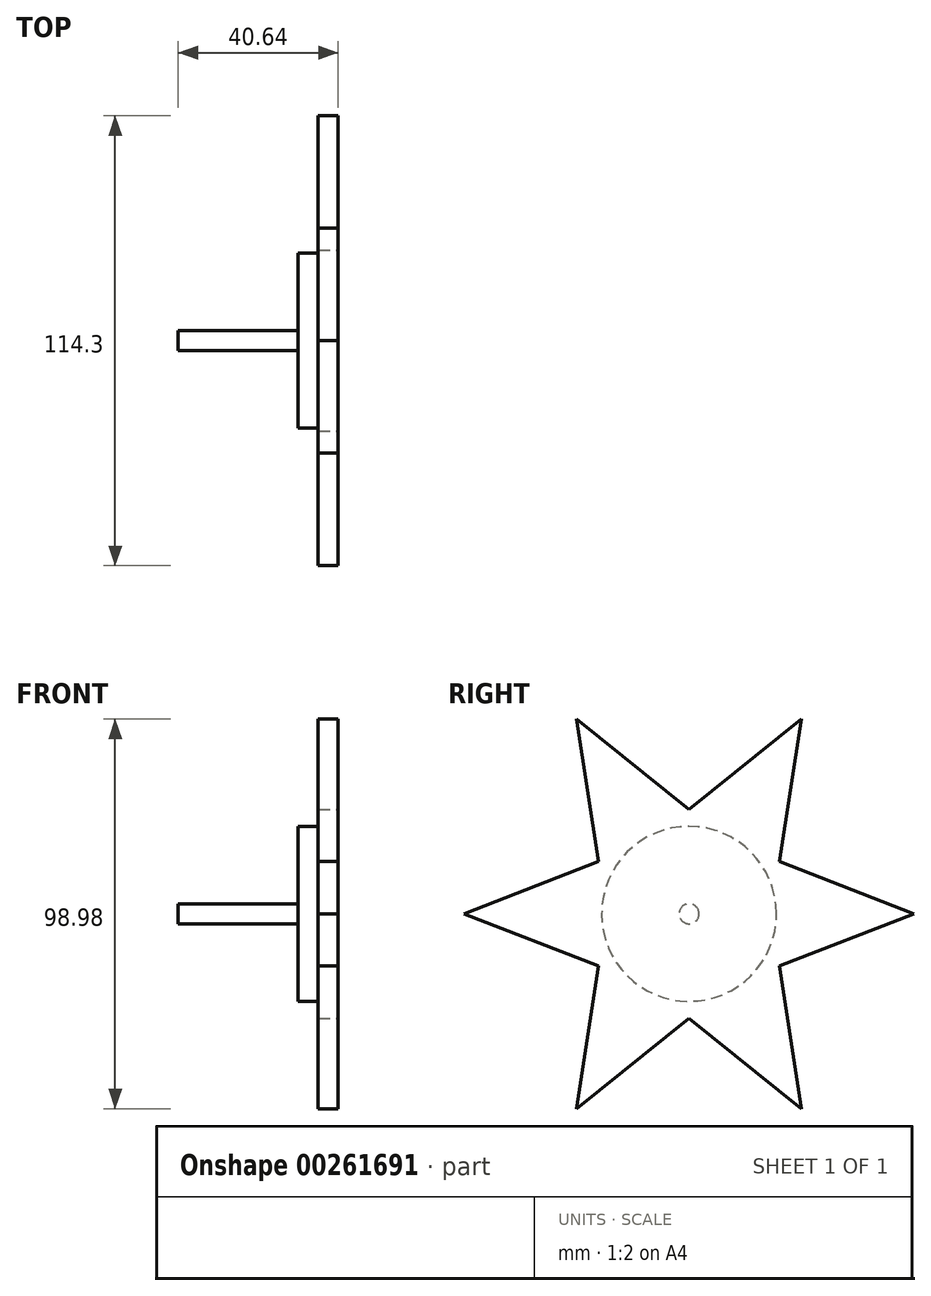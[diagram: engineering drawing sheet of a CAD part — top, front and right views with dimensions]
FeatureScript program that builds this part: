
annotation { "Feature Type Name" : "Feature", "Feature Type Description" : "" }
export const myFeature = defineFeature(function(context is Context, id is Id, definition is map)
    precondition{}
    {
        {
            var Q0;
            Q0=qCreatedBy(makeId("Right.planeOp"),FACE);
            var sketch = newSketch(context, id + "F0", { "sketchPlane" : qUnion([Q0])});
            skLineSegment(sketch, "E0", {"start": v(57.15, 0) * mm, "end": v(-57.15, 0) * mm});
            skCircle(sketch, "E1", {"center": v(0, 0) * mm, "radius": 2.54 * mm});
            skCircle(sketch, "E2", {"center": v(0, 0) * mm, "radius": 22.23 * mm});
            skCircle(sketch, "E3", {"center": v(0, 0) * mm, "radius": 57.15 * mm});
            skLineSegment(sketch, "E4", {"start": v(-57.15, 0) * mm, "end": v(0, 22.23) * mm});
            skLineSegment(sketch, "E5", {"start": v(0, 22.23) * mm, "end": v(57.15, 0) * mm});
            skLineSegment(sketch, "E6", {"start": v(57.15, 0) * mm, "end": v(0, -22.23) * mm});
            skLineSegment(sketch, "E7", {"start": v(0, -22.23) * mm, "end": v(-57.15, 0) * mm});
            skLineSegment(sketch, "E8", {"start": v(19.25, 11.11) * mm, "end": v(-28.57, 49.5) * mm});
            skLineSegment(sketch, "E9", {"start": v(-28.57, 49.5) * mm, "end": v(-19.25, -11.11) * mm});
            skLineSegment(sketch, "E10", {"start": v(-19.25, -11.11) * mm, "end": v(28.57, -49.5) * mm});
            skLineSegment(sketch, "E11", {"start": v(28.57, -49.5) * mm, "end": v(19.25, 11.11) * mm});
            skLineSegment(sketch, "E12", {"start": v(-28.57, 49.5) * mm, "end": v(28.57, -49.5) * mm});
            skLineSegment(sketch, "E13", {"start": v(-19.25, 11.11) * mm, "end": v(28.57, 49.5) * mm});
            skLineSegment(sketch, "E14", {"start": v(28.58, 49.5) * mm, "end": v(19.25, -11.11) * mm});
            skLineSegment(sketch, "E15", {"start": v(19.25, -11.11) * mm, "end": v(-28.58, -49.5) * mm});
            skLineSegment(sketch, "E16", {"start": v(-28.58, -49.5) * mm, "end": v(-19.25, 11.11) * mm});
            skLineSegment(sketch, "E17", {"start": v(28.57, 49.5) * mm, "end": v(-28.58, -49.5) * mm});
            skSolve(sketch);
        }
        {
            var Q0;
            {var subQ0=sQuery(id+"F0.wireOp",EDGE,"E1");var subQ1=sQuery(id+"F0.wireOp",EDGE,"E0");var subQ2=makeQuery(id+"F0.imprint","INTERSECT",VERTEX,{"disambiguationData":[OD(1.0)],"derivedFrom":[subQ1,subQ0]});Q0=makeQuery(id+"F0.imprint","IMPRINT",FACE,{"disambiguationData":[TD([[makeQuery(id+"F0.imprint","IMPRINT",EDGE,{"disambiguationData":[TD([[subQ2,-1.0]])],"derivedFrom":subQ0}),1.0]])]});}
            var Q1;
            {var subQ0=sQuery(id+"F0.wireOp",EDGE,"E17");var subQ1=sQuery(id+"F0.wireOp",EDGE,"E1");var subQ2=makeQuery(id+"F0.imprint","INTERSECT",VERTEX,{"disambiguationData":[OD(1.0)],"derivedFrom":[subQ1,subQ0]});Q1=makeQuery(id+"F0.imprint","IMPRINT",FACE,{"disambiguationData":[TD([[makeQuery(id+"F0.imprint","IMPRINT",EDGE,{"disambiguationData":[TD([[subQ2,-1.0]])],"derivedFrom":subQ1}),1.0]])]});}
            var Q2;
            {var subQ0=sQuery(id+"F0.wireOp",EDGE,"E1");var subQ1=sQuery(id+"F0.wireOp",EDGE,"E0");var subQ2=makeQuery(id+"F0.imprint","INTERSECT",VERTEX,{"disambiguationData":[OD(0.0)],"derivedFrom":[subQ1,subQ0]});Q2=makeQuery(id+"F0.imprint","IMPRINT",FACE,{"disambiguationData":[TD([[makeQuery(id+"F0.imprint","IMPRINT",EDGE,{"disambiguationData":[TD([[subQ2,1.0]])],"derivedFrom":subQ0}),1.0]])]});}
            var Q3;
            {var subQ0=sQuery(id+"F0.wireOp",EDGE,"E1");var subQ1=sQuery(id+"F0.wireOp",EDGE,"E0");var subQ2=makeQuery(id+"F0.imprint","INTERSECT",VERTEX,{"disambiguationData":[OD(0.0)],"derivedFrom":[subQ1,subQ0]});Q3=makeQuery(id+"F0.imprint","IMPRINT",FACE,{"disambiguationData":[TD([[makeQuery(id+"F0.imprint","IMPRINT",EDGE,{"disambiguationData":[TD([[subQ2,-1.0]])],"derivedFrom":subQ0}),1.0]])]});}
            var Q4;
            {var subQ0=sQuery(id+"F0.wireOp",EDGE,"E17");var subQ1=sQuery(id+"F0.wireOp",EDGE,"E1");var subQ2=makeQuery(id+"F0.imprint","INTERSECT",VERTEX,{"disambiguationData":[OD(0.0)],"derivedFrom":[subQ1,subQ0]});Q4=makeQuery(id+"F0.imprint","IMPRINT",FACE,{"disambiguationData":[TD([[makeQuery(id+"F0.imprint","IMPRINT",EDGE,{"disambiguationData":[TD([[subQ2,-1.0]])],"derivedFrom":subQ1}),1.0]])]});}
            var Q5;
            {var subQ0=sQuery(id+"F0.wireOp",EDGE,"E1");var subQ1=sQuery(id+"F0.wireOp",EDGE,"E0");var subQ2=makeQuery(id+"F0.imprint","INTERSECT",VERTEX,{"disambiguationData":[OD(1.0)],"derivedFrom":[subQ1,subQ0]});Q5=makeQuery(id+"F0.imprint","IMPRINT",FACE,{"disambiguationData":[TD([[makeQuery(id+"F0.imprint","IMPRINT",EDGE,{"disambiguationData":[TD([[subQ2,1.0]])],"derivedFrom":subQ0}),1.0]])]});}
            extrude(context, id + "F1", {"entities" : qUnion([Q0, Q1, Q2, Q3, Q4, Q5]), "oppositeDirection" : true, "depth" : 40.64 * mm});
        }
        {
            var Q0;
            {var subQ1=sQuery(id+"F0.wireOp",EDGE,"E2");var subQ3=sQuery(id+"F0.wireOp",EDGE,"E11");var subQ4=makeQuery(id+"F0.imprint","INTERSECT",VERTEX,{"derivedFrom":[subQ1,subQ3]});Q0=makeQuery(id+"F0.imprint","IMPRINT",FACE,{"disambiguationData":[TD([[makeQuery(id+"F0.imprint","IMPRINT",EDGE,{"disambiguationData":[TD([[subQ4,1.0]])],"derivedFrom":subQ1}),1.0]])]});}
            var Q1;
            {var subQ3=sQuery(id+"F0.wireOp",EDGE,"E0");var subQ6=sQuery(id+"F0.wireOp",EDGE,"E1");var subQ9=makeQuery(id+"F0.imprint","INTERSECT",VERTEX,{"disambiguationData":[OD(0.0)],"derivedFrom":[subQ3,subQ6]});Q1=makeQuery(id+"F0.imprint","IMPRINT",FACE,{"disambiguationData":[TD([[makeQuery(id+"F0.imprint","IMPRINT",EDGE,{"disambiguationData":[TD([[subQ9,1.0]])],"derivedFrom":subQ6}),-1.0]])]});}
            var Q2;
            {var subQ3=sQuery(id+"F0.wireOp",EDGE,"E0");var subQ7=sQuery(id+"F0.wireOp",EDGE,"E1");var subQ8=makeQuery(id+"F0.imprint","INTERSECT",VERTEX,{"disambiguationData":[OD(0.0)],"derivedFrom":[subQ3,subQ7]});Q2=makeQuery(id+"F0.imprint","IMPRINT",FACE,{"disambiguationData":[TD([[makeQuery(id+"F0.imprint","IMPRINT",EDGE,{"disambiguationData":[TD([[subQ8,-1.0]])],"derivedFrom":subQ7}),-1.0]])]});}
            var Q3;
            {var subQ5=sQuery(id+"F0.wireOp",EDGE,"E1");var subQ7=sQuery(id+"F0.wireOp",EDGE,"E0");var subQ8=makeQuery(id+"F0.imprint","INTERSECT",VERTEX,{"disambiguationData":[OD(1.0)],"derivedFrom":[subQ7,subQ5]});Q3=makeQuery(id+"F0.imprint","IMPRINT",FACE,{"disambiguationData":[TD([[makeQuery(id+"F0.imprint","IMPRINT",EDGE,{"disambiguationData":[TD([[subQ8,1.0]])],"derivedFrom":subQ5}),-1.0]])]});}
            var Q4;
            {var subQ1=sQuery(id+"F0.wireOp",EDGE,"E1");var subQ7=sQuery(id+"F0.wireOp",EDGE,"E17");var subQ9=makeQuery(id+"F0.imprint","INTERSECT",VERTEX,{"disambiguationData":[OD(0.0)],"derivedFrom":[subQ1,subQ7]});Q4=makeQuery(id+"F0.imprint","IMPRINT",FACE,{"disambiguationData":[TD([[makeQuery(id+"F0.imprint","IMPRINT",EDGE,{"disambiguationData":[TD([[subQ9,-1.0]])],"derivedFrom":subQ1}),-1.0]])]});}
            var Q5;
            {var subQ5=sQuery(id+"F0.wireOp",EDGE,"E0");var subQ7=sQuery(id+"F0.wireOp",EDGE,"E1");var subQ8=makeQuery(id+"F0.imprint","INTERSECT",VERTEX,{"disambiguationData":[OD(1.0)],"derivedFrom":[subQ5,subQ7]});Q5=makeQuery(id+"F0.imprint","IMPRINT",FACE,{"disambiguationData":[TD([[makeQuery(id+"F0.imprint","IMPRINT",EDGE,{"disambiguationData":[TD([[subQ8,-1.0]])],"derivedFrom":subQ7}),-1.0]])]});}
            var Q6;
            {var subQ1=sQuery(id+"F0.wireOp",EDGE,"E1");var subQ7=sQuery(id+"F0.wireOp",EDGE,"E17");var subQ9=makeQuery(id+"F0.imprint","INTERSECT",VERTEX,{"disambiguationData":[OD(1.0)],"derivedFrom":[subQ1,subQ7]});Q6=makeQuery(id+"F0.imprint","IMPRINT",FACE,{"disambiguationData":[TD([[makeQuery(id+"F0.imprint","IMPRINT",EDGE,{"disambiguationData":[TD([[subQ9,-1.0]])],"derivedFrom":subQ1}),-1.0]])]});}
            var Q7;
            {var subQ0=sQuery(id+"F0.wireOp",EDGE,"E2");var subQ1=sQuery(id+"F0.wireOp",EDGE,"E0");var subQ2=makeQuery(id+"F0.imprint","INTERSECT",VERTEX,{"disambiguationData":[OD(0.0)],"derivedFrom":[subQ1,subQ0]});Q7=makeQuery(id+"F0.imprint","IMPRINT",FACE,{"disambiguationData":[TD([[makeQuery(id+"F0.imprint","IMPRINT",EDGE,{"disambiguationData":[TD([[subQ2,1.0]])],"derivedFrom":subQ0}),1.0]])]});}
            var Q8;
            {var subQ0=sQuery(id+"F0.wireOp",EDGE,"E2");var subQ1=sQuery(id+"F0.wireOp",EDGE,"E0");var subQ2=makeQuery(id+"F0.imprint","INTERSECT",VERTEX,{"disambiguationData":[OD(0.0)],"derivedFrom":[subQ1,subQ0]});Q8=makeQuery(id+"F0.imprint","IMPRINT",FACE,{"disambiguationData":[TD([[makeQuery(id+"F0.imprint","IMPRINT",EDGE,{"disambiguationData":[TD([[subQ2,-1.0]])],"derivedFrom":subQ0}),1.0]])]});}
            var Q9;
            {var subQ1=sQuery(id+"F0.wireOp",EDGE,"E2");var subQ3=sQuery(id+"F0.wireOp",EDGE,"E14");var subQ4=makeQuery(id+"F0.imprint","INTERSECT",VERTEX,{"derivedFrom":[subQ1,subQ3]});Q9=makeQuery(id+"F0.imprint","IMPRINT",FACE,{"disambiguationData":[TD([[makeQuery(id+"F0.imprint","IMPRINT",EDGE,{"disambiguationData":[TD([[subQ4,-1.0]])],"derivedFrom":subQ1}),1.0]])]});}
            var Q10;
            {var subQ1=sQuery(id+"F0.wireOp",EDGE,"E2");var subQ3=sQuery(id+"F0.wireOp",EDGE,"E5");var subQ4=makeQuery(id+"F0.imprint","INTERSECT",VERTEX,{"derivedFrom":[subQ1,subQ3]});Q10=makeQuery(id+"F0.imprint","IMPRINT",FACE,{"disambiguationData":[TD([[makeQuery(id+"F0.imprint","IMPRINT",EDGE,{"disambiguationData":[TD([[subQ4,1.0]])],"derivedFrom":subQ1}),1.0]])]});}
            var Q11;
            {var subQ0=sQuery(id+"F0.wireOp",EDGE,"E5");var subQ1=sQuery(id+"F0.wireOp",EDGE,"E2");var subQ2=makeQuery(id+"F0.imprint","INTERSECT",VERTEX,{"derivedFrom":[subQ1,subQ0]});Q11=makeQuery(id+"F0.imprint","IMPRINT",FACE,{"disambiguationData":[TD([[makeQuery(id+"F0.imprint","IMPRINT",EDGE,{"disambiguationData":[TD([[subQ2,-1.0]])],"derivedFrom":subQ1}),1.0]])]});}
            var Q12;
            {var subQ0=sQuery(id+"F0.wireOp",EDGE,"E17");var subQ1=sQuery(id+"F0.wireOp",EDGE,"E2");var subQ2=makeQuery(id+"F0.imprint","INTERSECT",VERTEX,{"disambiguationData":[OD(0.0)],"derivedFrom":[subQ1,subQ0]});Q12=makeQuery(id+"F0.imprint","IMPRINT",FACE,{"disambiguationData":[TD([[makeQuery(id+"F0.imprint","IMPRINT",EDGE,{"disambiguationData":[TD([[subQ2,-1.0]])],"derivedFrom":subQ1}),1.0]])]});}
            var Q13;
            {var subQ1=sQuery(id+"F0.wireOp",EDGE,"E2");var subQ3=sQuery(id+"F0.wireOp",EDGE,"E8");var subQ4=makeQuery(id+"F0.imprint","INTERSECT",VERTEX,{"derivedFrom":[subQ1,subQ3]});Q13=makeQuery(id+"F0.imprint","IMPRINT",FACE,{"disambiguationData":[TD([[makeQuery(id+"F0.imprint","IMPRINT",EDGE,{"disambiguationData":[TD([[subQ4,-1.0]])],"derivedFrom":subQ1}),1.0]])]});}
            var Q14;
            {var subQ1=sQuery(id+"F0.wireOp",EDGE,"E2");var subQ3=sQuery(id+"F0.wireOp",EDGE,"E13");var subQ4=makeQuery(id+"F0.imprint","INTERSECT",VERTEX,{"derivedFrom":[subQ1,subQ3]});Q14=makeQuery(id+"F0.imprint","IMPRINT",FACE,{"disambiguationData":[TD([[makeQuery(id+"F0.imprint","IMPRINT",EDGE,{"disambiguationData":[TD([[subQ4,1.0]])],"derivedFrom":subQ1}),1.0]])]});}
            var Q15;
            {var subQ0=sQuery(id+"F0.wireOp",EDGE,"E13");var subQ1=sQuery(id+"F0.wireOp",EDGE,"E2");var subQ2=makeQuery(id+"F0.imprint","INTERSECT",VERTEX,{"derivedFrom":[subQ1,subQ0]});Q15=makeQuery(id+"F0.imprint","IMPRINT",FACE,{"disambiguationData":[TD([[makeQuery(id+"F0.imprint","IMPRINT",EDGE,{"disambiguationData":[TD([[subQ2,-1.0]])],"derivedFrom":subQ1}),1.0]])]});}
            var Q16;
            {var subQ0=sQuery(id+"F0.wireOp",EDGE,"E12");var subQ1=sQuery(id+"F0.wireOp",EDGE,"E2");var subQ2=makeQuery(id+"F0.imprint","INTERSECT",VERTEX,{"disambiguationData":[OD(0.0)],"derivedFrom":[subQ1,subQ0]});Q16=makeQuery(id+"F0.imprint","IMPRINT",FACE,{"disambiguationData":[TD([[makeQuery(id+"F0.imprint","IMPRINT",EDGE,{"disambiguationData":[TD([[subQ2,-1.0]])],"derivedFrom":subQ1}),1.0]])]});}
            var Q17;
            {var subQ1=sQuery(id+"F0.wireOp",EDGE,"E2");var subQ3=sQuery(id+"F0.wireOp",EDGE,"E4");var subQ4=makeQuery(id+"F0.imprint","INTERSECT",VERTEX,{"derivedFrom":[subQ1,subQ3]});Q17=makeQuery(id+"F0.imprint","IMPRINT",FACE,{"disambiguationData":[TD([[makeQuery(id+"F0.imprint","IMPRINT",EDGE,{"disambiguationData":[TD([[subQ4,-1.0]])],"derivedFrom":subQ1}),1.0]])]});}
            var Q18;
            {var subQ1=sQuery(id+"F0.wireOp",EDGE,"E2");var subQ3=sQuery(id+"F0.wireOp",EDGE,"E9");var subQ4=makeQuery(id+"F0.imprint","INTERSECT",VERTEX,{"derivedFrom":[subQ1,subQ3]});Q18=makeQuery(id+"F0.imprint","IMPRINT",FACE,{"disambiguationData":[TD([[makeQuery(id+"F0.imprint","IMPRINT",EDGE,{"disambiguationData":[TD([[subQ4,1.0]])],"derivedFrom":subQ1}),1.0]])]});}
            var Q19;
            {var subQ0=sQuery(id+"F0.wireOp",EDGE,"E2");var subQ1=sQuery(id+"F0.wireOp",EDGE,"E0");var subQ2=makeQuery(id+"F0.imprint","INTERSECT",VERTEX,{"disambiguationData":[OD(1.0)],"derivedFrom":[subQ1,subQ0]});Q19=makeQuery(id+"F0.imprint","IMPRINT",FACE,{"disambiguationData":[TD([[makeQuery(id+"F0.imprint","IMPRINT",EDGE,{"disambiguationData":[TD([[subQ2,1.0]])],"derivedFrom":subQ0}),1.0]])]});}
            var Q20;
            {var subQ1=sQuery(id+"F0.wireOp",EDGE,"E2");var subQ3=sQuery(id+"F0.wireOp",EDGE,"E16");var subQ4=makeQuery(id+"F0.imprint","INTERSECT",VERTEX,{"derivedFrom":[subQ1,subQ3]});Q20=makeQuery(id+"F0.imprint","IMPRINT",FACE,{"disambiguationData":[TD([[makeQuery(id+"F0.imprint","IMPRINT",EDGE,{"disambiguationData":[TD([[subQ4,-1.0]])],"derivedFrom":subQ1}),1.0]])]});}
            var Q21;
            {var subQ0=sQuery(id+"F0.wireOp",EDGE,"E2");var subQ1=sQuery(id+"F0.wireOp",EDGE,"E0");var subQ2=makeQuery(id+"F0.imprint","INTERSECT",VERTEX,{"disambiguationData":[OD(1.0)],"derivedFrom":[subQ1,subQ0]});Q21=makeQuery(id+"F0.imprint","IMPRINT",FACE,{"disambiguationData":[TD([[makeQuery(id+"F0.imprint","IMPRINT",EDGE,{"disambiguationData":[TD([[subQ2,-1.0]])],"derivedFrom":subQ0}),1.0]])]});}
            var Q22;
            {var subQ1=sQuery(id+"F0.wireOp",EDGE,"E2");var subQ3=sQuery(id+"F0.wireOp",EDGE,"E6");var subQ4=makeQuery(id+"F0.imprint","INTERSECT",VERTEX,{"derivedFrom":[subQ1,subQ3]});Q22=makeQuery(id+"F0.imprint","IMPRINT",FACE,{"disambiguationData":[TD([[makeQuery(id+"F0.imprint","IMPRINT",EDGE,{"disambiguationData":[TD([[subQ4,-1.0]])],"derivedFrom":subQ1}),1.0]])]});}
            var Q23;
            {var subQ0=sQuery(id+"F0.wireOp",EDGE,"E12");var subQ1=sQuery(id+"F0.wireOp",EDGE,"E2");var subQ2=makeQuery(id+"F0.imprint","INTERSECT",VERTEX,{"disambiguationData":[OD(1.0)],"derivedFrom":[subQ1,subQ0]});Q23=makeQuery(id+"F0.imprint","IMPRINT",FACE,{"disambiguationData":[TD([[makeQuery(id+"F0.imprint","IMPRINT",EDGE,{"disambiguationData":[TD([[subQ2,-1.0]])],"derivedFrom":subQ1}),1.0]])]});}
            var Q24;
            {var subQ0=sQuery(id+"F0.wireOp",EDGE,"E15");var subQ1=sQuery(id+"F0.wireOp",EDGE,"E2");var subQ2=makeQuery(id+"F0.imprint","INTERSECT",VERTEX,{"derivedFrom":[subQ1,subQ0]});Q24=makeQuery(id+"F0.imprint","IMPRINT",FACE,{"disambiguationData":[TD([[makeQuery(id+"F0.imprint","IMPRINT",EDGE,{"disambiguationData":[TD([[subQ2,-1.0]])],"derivedFrom":subQ1}),1.0]])]});}
            var Q25;
            {var subQ1=sQuery(id+"F0.wireOp",EDGE,"E2");var subQ3=sQuery(id+"F0.wireOp",EDGE,"E15");var subQ4=makeQuery(id+"F0.imprint","INTERSECT",VERTEX,{"derivedFrom":[subQ1,subQ3]});Q25=makeQuery(id+"F0.imprint","IMPRINT",FACE,{"disambiguationData":[TD([[makeQuery(id+"F0.imprint","IMPRINT",EDGE,{"disambiguationData":[TD([[subQ4,1.0]])],"derivedFrom":subQ1}),1.0]])]});}
            var Q26;
            {var subQ1=sQuery(id+"F0.wireOp",EDGE,"E2");var subQ3=sQuery(id+"F0.wireOp",EDGE,"E10");var subQ4=makeQuery(id+"F0.imprint","INTERSECT",VERTEX,{"derivedFrom":[subQ1,subQ3]});Q26=makeQuery(id+"F0.imprint","IMPRINT",FACE,{"disambiguationData":[TD([[makeQuery(id+"F0.imprint","IMPRINT",EDGE,{"disambiguationData":[TD([[subQ4,-1.0]])],"derivedFrom":subQ1}),1.0]])]});}
            var Q27;
            {var subQ0=sQuery(id+"F0.wireOp",EDGE,"E17");var subQ1=sQuery(id+"F0.wireOp",EDGE,"E2");var subQ2=makeQuery(id+"F0.imprint","INTERSECT",VERTEX,{"disambiguationData":[OD(1.0)],"derivedFrom":[subQ1,subQ0]});Q27=makeQuery(id+"F0.imprint","IMPRINT",FACE,{"disambiguationData":[TD([[makeQuery(id+"F0.imprint","IMPRINT",EDGE,{"disambiguationData":[TD([[subQ2,-1.0]])],"derivedFrom":subQ1}),1.0]])]});}
            var Q28;
            {var subQ0=sQuery(id+"F0.wireOp",EDGE,"E7");var subQ1=sQuery(id+"F0.wireOp",EDGE,"E2");var subQ2=makeQuery(id+"F0.imprint","INTERSECT",VERTEX,{"derivedFrom":[subQ1,subQ0]});Q28=makeQuery(id+"F0.imprint","IMPRINT",FACE,{"disambiguationData":[TD([[makeQuery(id+"F0.imprint","IMPRINT",EDGE,{"disambiguationData":[TD([[subQ2,-1.0]])],"derivedFrom":subQ1}),1.0]])]});}
            var Q29;
            {var subQ1=sQuery(id+"F0.wireOp",EDGE,"E2");var subQ3=sQuery(id+"F0.wireOp",EDGE,"E7");var subQ4=makeQuery(id+"F0.imprint","INTERSECT",VERTEX,{"derivedFrom":[subQ1,subQ3]});Q29=makeQuery(id+"F0.imprint","IMPRINT",FACE,{"disambiguationData":[TD([[makeQuery(id+"F0.imprint","IMPRINT",EDGE,{"disambiguationData":[TD([[subQ4,1.0]])],"derivedFrom":subQ1}),1.0]])]});}
            extrude(context, id + "F2", {"entities" : qUnion([Q0, Q1, Q2, Q3, Q4, Q5, Q6, Q7, Q8, Q9, Q10, Q11, Q12, Q13, Q14, Q15, Q16, Q17, Q18, Q19, Q20, Q21, Q22, Q23, Q24, Q25, Q26, Q27, Q28, Q29]), "operationType" : NewBodyOperationType.ADD, "oppositeDirection" : true, "depth" : 10.16 * mm});
        }
        {
            var Q0;
            {var subQ0=sQuery(id+"F0.wireOp",EDGE,"E2");var subQ2=sQuery(id+"F0.wireOp",EDGE,"E6");var subQ3=makeQuery(id+"F0.imprint","INTERSECT",VERTEX,{"derivedFrom":[subQ0,subQ2]});Q0=makeQuery(id+"F0.imprint","IMPRINT",FACE,{"disambiguationData":[TD([[makeQuery(id+"F0.imprint","IMPRINT",EDGE,{"disambiguationData":[TD([[subQ3,1.0]])],"derivedFrom":subQ2}),-1.0]])]});}
            var Q1;
            {var subQ0=sQuery(id+"F0.wireOp",EDGE,"E12");var subQ1=sQuery(id+"F0.wireOp",EDGE,"E2");var subQ2=makeQuery(id+"F0.imprint","INTERSECT",VERTEX,{"disambiguationData":[OD(1.0)],"derivedFrom":[subQ1,subQ0]});Q1=makeQuery(id+"F0.imprint","IMPRINT",FACE,{"disambiguationData":[TD([[makeQuery(id+"F0.imprint","IMPRINT",EDGE,{"disambiguationData":[TD([[subQ2,-1.0]])],"derivedFrom":subQ1}),-1.0]])]});}
            var Q2;
            {var subQ0=sQuery(id+"F0.wireOp",EDGE,"E15");var subQ1=sQuery(id+"F0.wireOp",EDGE,"E2");var subQ2=makeQuery(id+"F0.imprint","INTERSECT",VERTEX,{"derivedFrom":[subQ1,subQ0]});Q2=makeQuery(id+"F0.imprint","IMPRINT",FACE,{"disambiguationData":[TD([[makeQuery(id+"F0.imprint","IMPRINT",EDGE,{"disambiguationData":[TD([[subQ2,-1.0]])],"derivedFrom":subQ1}),-1.0]])]});}
            var Q3;
            {var subQ0=sQuery(id+"F0.wireOp",EDGE,"E2");var subQ2=sQuery(id+"F0.wireOp",EDGE,"E10");var subQ3=makeQuery(id+"F0.imprint","INTERSECT",VERTEX,{"derivedFrom":[subQ0,subQ2]});Q3=makeQuery(id+"F0.imprint","IMPRINT",FACE,{"disambiguationData":[TD([[makeQuery(id+"F0.imprint","IMPRINT",EDGE,{"disambiguationData":[TD([[subQ3,-1.0]])],"derivedFrom":subQ2}),1.0]])]});}
            var Q4;
            {var subQ0=sQuery(id+"F0.wireOp",EDGE,"E17");var subQ1=sQuery(id+"F0.wireOp",EDGE,"E2");var subQ2=makeQuery(id+"F0.imprint","INTERSECT",VERTEX,{"disambiguationData":[OD(1.0)],"derivedFrom":[subQ1,subQ0]});Q4=makeQuery(id+"F0.imprint","IMPRINT",FACE,{"disambiguationData":[TD([[makeQuery(id+"F0.imprint","IMPRINT",EDGE,{"disambiguationData":[TD([[subQ2,-1.0]])],"derivedFrom":subQ1}),-1.0]])]});}
            var Q5;
            {var subQ0=sQuery(id+"F0.wireOp",EDGE,"E7");var subQ1=sQuery(id+"F0.wireOp",EDGE,"E2");var subQ2=makeQuery(id+"F0.imprint","INTERSECT",VERTEX,{"derivedFrom":[subQ1,subQ0]});Q5=makeQuery(id+"F0.imprint","IMPRINT",FACE,{"disambiguationData":[TD([[makeQuery(id+"F0.imprint","IMPRINT",EDGE,{"disambiguationData":[TD([[subQ2,-1.0]])],"derivedFrom":subQ1}),-1.0]])]});}
            var Q6;
            {var subQ0=sQuery(id+"F0.wireOp",EDGE,"E2");var subQ4=sQuery(id+"F0.wireOp",EDGE,"E7");var subQ6=makeQuery(id+"F0.imprint","INTERSECT",VERTEX,{"derivedFrom":[subQ0,subQ4]});Q6=makeQuery(id+"F0.imprint","IMPRINT",FACE,{"disambiguationData":[TD([[makeQuery(id+"F0.imprint","IMPRINT",EDGE,{"disambiguationData":[TD([[subQ6,-1.0]])],"derivedFrom":subQ4}),-1.0]])]});}
            var Q7;
            {var subQ1=sQuery(id+"F0.wireOp",EDGE,"E0");var subQ3=sQuery(id+"F0.wireOp",EDGE,"E2");var subQ4=makeQuery(id+"F0.imprint","INTERSECT",VERTEX,{"disambiguationData":[OD(1.0)],"derivedFrom":[subQ1,subQ3]});Q7=makeQuery(id+"F0.imprint","IMPRINT",FACE,{"disambiguationData":[TD([[makeQuery(id+"F0.imprint","IMPRINT",EDGE,{"disambiguationData":[TD([[subQ4,-1.0]])],"derivedFrom":subQ3}),-1.0]])]});}
            var Q8;
            {var subQ1=sQuery(id+"F0.wireOp",EDGE,"E0");var subQ3=sQuery(id+"F0.wireOp",EDGE,"E2");var subQ4=makeQuery(id+"F0.imprint","INTERSECT",VERTEX,{"disambiguationData":[OD(1.0)],"derivedFrom":[subQ1,subQ3]});Q8=makeQuery(id+"F0.imprint","IMPRINT",FACE,{"disambiguationData":[TD([[makeQuery(id+"F0.imprint","IMPRINT",EDGE,{"disambiguationData":[TD([[subQ4,1.0]])],"derivedFrom":subQ3}),-1.0]])]});}
            var Q9;
            {var subQ0=sQuery(id+"F0.wireOp",EDGE,"E2");var subQ2=sQuery(id+"F0.wireOp",EDGE,"E4");var subQ3=makeQuery(id+"F0.imprint","INTERSECT",VERTEX,{"derivedFrom":[subQ0,subQ2]});Q9=makeQuery(id+"F0.imprint","IMPRINT",FACE,{"disambiguationData":[TD([[makeQuery(id+"F0.imprint","IMPRINT",EDGE,{"disambiguationData":[TD([[subQ3,1.0]])],"derivedFrom":subQ2}),-1.0]])]});}
            var Q10;
            {var subQ0=sQuery(id+"F0.wireOp",EDGE,"E12");var subQ1=sQuery(id+"F0.wireOp",EDGE,"E2");var subQ2=makeQuery(id+"F0.imprint","INTERSECT",VERTEX,{"disambiguationData":[OD(0.0)],"derivedFrom":[subQ1,subQ0]});Q10=makeQuery(id+"F0.imprint","IMPRINT",FACE,{"disambiguationData":[TD([[makeQuery(id+"F0.imprint","IMPRINT",EDGE,{"disambiguationData":[TD([[subQ2,-1.0]])],"derivedFrom":subQ1}),-1.0]])]});}
            var Q11;
            {var subQ0=sQuery(id+"F0.wireOp",EDGE,"E13");var subQ1=sQuery(id+"F0.wireOp",EDGE,"E2");var subQ2=makeQuery(id+"F0.imprint","INTERSECT",VERTEX,{"derivedFrom":[subQ1,subQ0]});Q11=makeQuery(id+"F0.imprint","IMPRINT",FACE,{"disambiguationData":[TD([[makeQuery(id+"F0.imprint","IMPRINT",EDGE,{"disambiguationData":[TD([[subQ2,-1.0]])],"derivedFrom":subQ1}),-1.0]])]});}
            var Q12;
            {var subQ0=sQuery(id+"F0.wireOp",EDGE,"E2");var subQ2=sQuery(id+"F0.wireOp",EDGE,"E8");var subQ3=makeQuery(id+"F0.imprint","INTERSECT",VERTEX,{"derivedFrom":[subQ0,subQ2]});Q12=makeQuery(id+"F0.imprint","IMPRINT",FACE,{"disambiguationData":[TD([[makeQuery(id+"F0.imprint","IMPRINT",EDGE,{"disambiguationData":[TD([[subQ3,-1.0]])],"derivedFrom":subQ2}),1.0]])]});}
            var Q13;
            {var subQ0=sQuery(id+"F0.wireOp",EDGE,"E17");var subQ1=sQuery(id+"F0.wireOp",EDGE,"E2");var subQ2=makeQuery(id+"F0.imprint","INTERSECT",VERTEX,{"disambiguationData":[OD(0.0)],"derivedFrom":[subQ1,subQ0]});Q13=makeQuery(id+"F0.imprint","IMPRINT",FACE,{"disambiguationData":[TD([[makeQuery(id+"F0.imprint","IMPRINT",EDGE,{"disambiguationData":[TD([[subQ2,-1.0]])],"derivedFrom":subQ1}),-1.0]])]});}
            var Q14;
            {var subQ1=sQuery(id+"F0.wireOp",EDGE,"E0");var subQ3=sQuery(id+"F0.wireOp",EDGE,"E2");var subQ4=makeQuery(id+"F0.imprint","INTERSECT",VERTEX,{"disambiguationData":[OD(0.0)],"derivedFrom":[subQ1,subQ3]});Q14=makeQuery(id+"F0.imprint","IMPRINT",FACE,{"disambiguationData":[TD([[makeQuery(id+"F0.imprint","IMPRINT",EDGE,{"disambiguationData":[TD([[subQ4,1.0]])],"derivedFrom":subQ3}),-1.0]])]});}
            var Q15;
            {var subQ1=sQuery(id+"F0.wireOp",EDGE,"E0");var subQ3=sQuery(id+"F0.wireOp",EDGE,"E2");var subQ4=makeQuery(id+"F0.imprint","INTERSECT",VERTEX,{"disambiguationData":[OD(0.0)],"derivedFrom":[subQ1,subQ3]});Q15=makeQuery(id+"F0.imprint","IMPRINT",FACE,{"disambiguationData":[TD([[makeQuery(id+"F0.imprint","IMPRINT",EDGE,{"disambiguationData":[TD([[subQ4,-1.0]])],"derivedFrom":subQ3}),-1.0]])]});}
            var Q16;
            {var subQ0=sQuery(id+"F0.wireOp",EDGE,"E2");var subQ4=sQuery(id+"F0.wireOp",EDGE,"E5");var subQ5=makeQuery(id+"F0.imprint","INTERSECT",VERTEX,{"derivedFrom":[subQ0,subQ4]});Q16=makeQuery(id+"F0.imprint","IMPRINT",FACE,{"disambiguationData":[TD([[makeQuery(id+"F0.imprint","IMPRINT",EDGE,{"disambiguationData":[TD([[subQ5,-1.0]])],"derivedFrom":subQ4}),-1.0]])]});}
            var Q17;
            {var subQ0=sQuery(id+"F0.wireOp",EDGE,"E5");var subQ1=sQuery(id+"F0.wireOp",EDGE,"E2");var subQ2=makeQuery(id+"F0.imprint","INTERSECT",VERTEX,{"derivedFrom":[subQ1,subQ0]});Q17=makeQuery(id+"F0.imprint","IMPRINT",FACE,{"disambiguationData":[TD([[makeQuery(id+"F0.imprint","IMPRINT",EDGE,{"disambiguationData":[TD([[subQ2,-1.0]])],"derivedFrom":subQ1}),-1.0]])]});}
            extrude(context, id + "F3", {"entities" : qUnion([Q0, Q1, Q2, Q3, Q4, Q5, Q6, Q7, Q8, Q9, Q10, Q11, Q12, Q13, Q14, Q15, Q16, Q17]), "operationType" : NewBodyOperationType.ADD, "oppositeDirection" : true, "depth" : 5.08 * mm});
        }
    });
